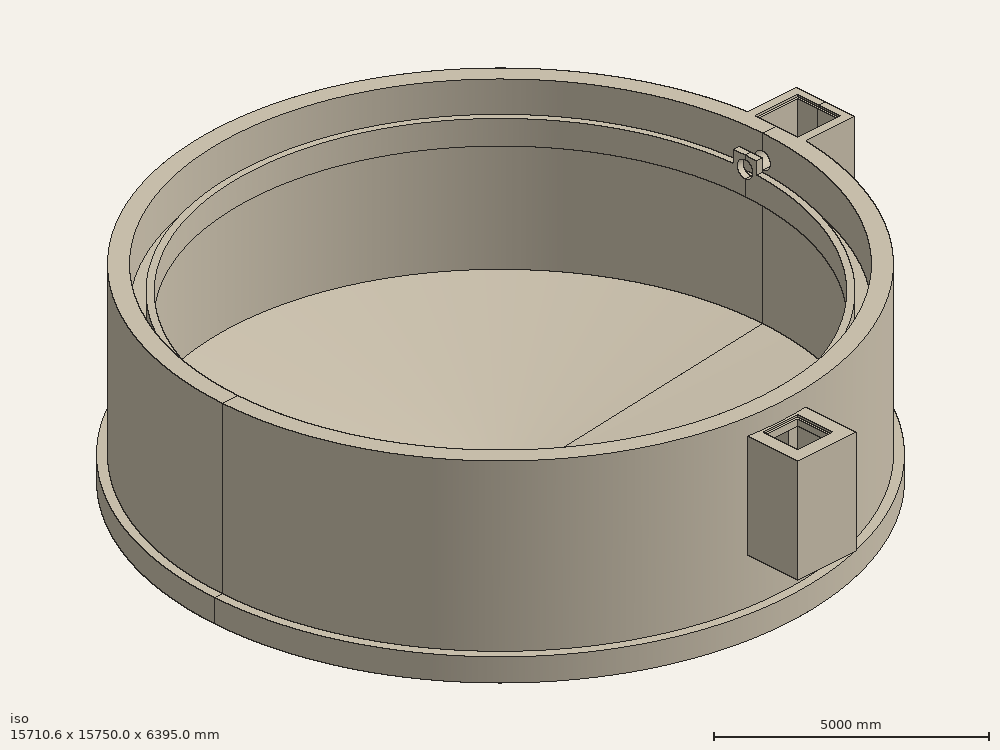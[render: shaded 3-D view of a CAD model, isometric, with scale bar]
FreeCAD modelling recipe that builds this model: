
FCSTD DOCUMENT  (FreeCAD 1.0R39109 (Git))
Label: body13.5m
License: All rights reserved
LicenseURL: https://en.wikipedia.org/wiki/All_rights_reserved
objects: Part::Feature×3, Part::FeaturePython×3, Part::MultiFuse×1, Part::Part2DObjectPython×1, App::DocumentObjectGroup×1, App::Part×1
note: 8 computed .brp shape members not serialized (recipe doc carries the construction recipe); baked Part::Feature solids carry a one-line shape summary decoded from their .brp

FEATURE [Part::Feature] Part__Feature  label="\X2\7D426C888EAF4F5353F3\X0\_1100 v12"
  shape: bbox 15710 x 15750 x 6395 mm, 63 faces (baked)
FEATURE [Part::Feature] Part__Feature001  label="\X2\7D426C888EAF4F5353F3\X0\_1100 v013"
  shape: bbox 1000 x 1000 x 130.8 mm, 5 faces (baked)
FEATURE [Part::Feature] Part__Feature002  label="\X2\7D426C888EAF4F5353F3\X0\_1100 v014"
  shape: bbox 1000 x 1000 x 105 mm, 5 faces (baked)
FEATURE [Part::MultiFuse] Fusion
  Refine = true
  Shapes = -> [Part__Feature,Part__Feature001,Part__Feature002]
FEATURE [Part::Part2DObjectPython] Rectangle  # Draft 2D object (typed FeaturePython)
  Area = 1.5232e+08
  ChamferSize = 0
  Columns = 1
  FilletRadius = 0
  Height = 8975.74
  Length = 16970.2
  MakeFace = true
  Placement = pos=(-8023.13,4.014e-13,-1958.45) rot=(1,0,0;1.5708rad)
  Rows = 1
FEATURE [Part::FeaturePython] Slice  # WARN: FeaturePython — macro-defined, semantics opaque (R4)
  Base = -> Fusion
  Mode = 1
  Tolerance = 0
  Tools = -> [Rectangle]
FEATURE [Part::FeaturePython] Slice_child0  label="Slice.0"  # WARN: FeaturePython — macro-defined, semantics opaque (R4)
  Base = -> Slice
  FilterType = 1
  Invert = false
  OverrideMaxVal = 0
  WindowFrom = 80
  WindowTo = 100
  items = 0
FEATURE [Part::FeaturePython] Slice_child1  label="Slice.1"  # WARN: FeaturePython — macro-defined, semantics opaque (R4)
  Base = -> Slice
  FilterType = 1
  Invert = false
  OverrideMaxVal = 0
  WindowFrom = 80
  WindowTo = 100
  items = 1
FEATURE [App::DocumentObjectGroup] GrExplode_Slice  label="Exploded Slice"
  Group = -> [Slice_child0,Slice_child1]
FEATURE [App::Part] _X2_7D426C888EAF4F5353F3_X0__1100_v12  label="body13.5m"
  Group = -> [Part__Feature,Part__Feature001,Part__Feature002,Fusion,Rectangle,Slice_child1,Slice,Slice_child0,GrExplode_Slice]
  Origin = -> Origin
